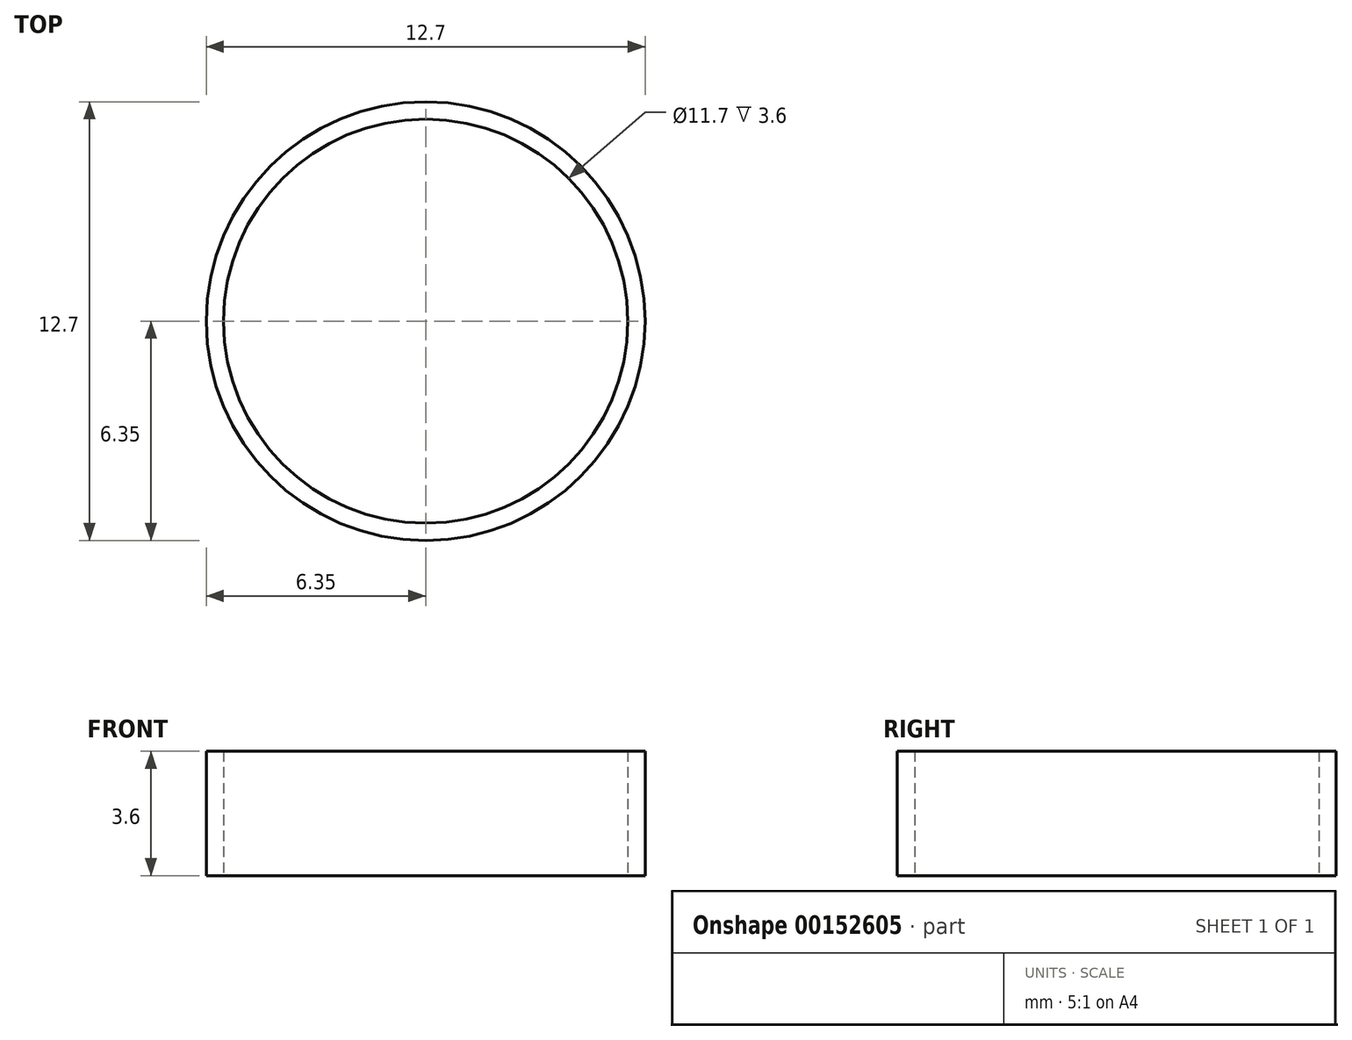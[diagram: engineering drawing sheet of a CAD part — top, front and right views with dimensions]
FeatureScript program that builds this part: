
annotation { "Feature Type Name" : "Feature", "Feature Type Description" : "" }
export const myFeature = defineFeature(function(context is Context, id is Id, definition is map)
    precondition{}
    {
        {
            var Q0;
            Q0=qCreatedBy(makeId("Top.planeOp"),FACE);
            var sketch = newSketch(context, id + "F0", { "sketchPlane" : qUnion([Q0])});
            skCircle(sketch, "E0", {"center": v(0, 0) * mm, "radius": 6.35 * mm});
            skCircle(sketch, "E1", {"center": v(0, 0) * mm, "radius": 5.85 * mm});
            skSolve(sketch);
        }
        {
            var Q0;
            Q0=makeQuery(id+"F0.imprint","IMPRINT",FACE,{"disambiguationData":[TD([[makeQuery(id+"F0.imprint","IMPRINT",EDGE,{"derivedFrom":sQuery(id+"F0.wireOp",EDGE,"E0")}),1.0]])]});
            extrude(context, id + "F1", {"entities" : qUnion([Q0]), "depth" : 3.6 * mm});
        }
    });
